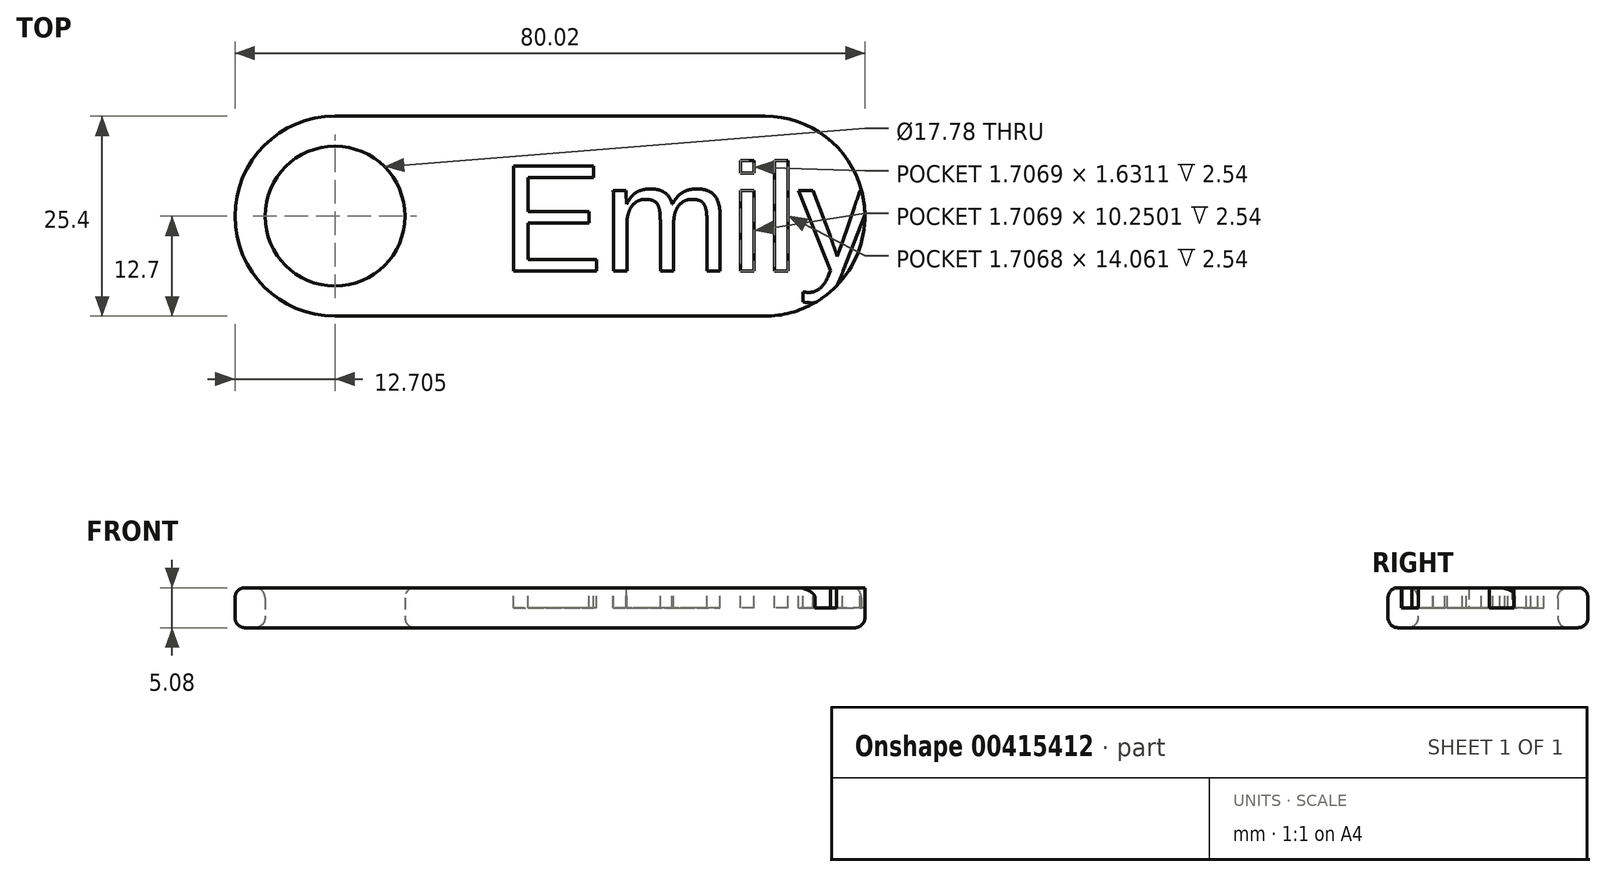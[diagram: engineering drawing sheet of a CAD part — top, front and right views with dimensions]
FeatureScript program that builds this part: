
annotation { "Feature Type Name" : "Feature", "Feature Type Description" : "" }
export const myFeature = defineFeature(function(context is Context, id is Id, definition is map)
    precondition{}
    {
        {
            var Q0;
            Q0=qCreatedBy(makeId("Top.planeOp"),FACE);
            var sketch = newSketch(context, id + "F0", { "sketchPlane" : qUnion([Q0])});
            skLineSegment(sketch, "E0.bottom", {"start": v(27.3, -12.7) * mm, "end": v(-27.3, -12.7) * mm});
            skLineSegment(sketch, "E0.top", {"start": v(27.3, 12.7) * mm, "end": v(-27.3, 12.7) * mm});
            skPoint(sketch, "E0.middle", {"position": v(0, 0) * mm});
            skArc(sketch, "E1", {"start": v(27.3, -12.7) * mm, "mid": v(40, 0) * mm, "end": v(27.3, 12.7) * mm});
            skArc(sketch, "E2", {"start": v(-27.3, 12.7) * mm, "mid": v(-40, 0) * mm, "end": v(-27.3, -12.7) * mm});
            skCircle(sketch, "E3", {"center": v(-27.3, 0) * mm, "radius": 8.9 * mm});
            skSolve(sketch);
        }
        {
            var Q0;
            Q0=makeQuery(id+"F0.imprint","IMPRINT",FACE,{"disambiguationData":[TD([[makeQuery(id+"F0.imprint","IMPRINT",EDGE,{"derivedFrom":sQuery(id+"F0.wireOp",EDGE,"E0.bottom")}),-1.0]])]});
            extrude(context, id + "F1", {"entities" : qUnion([Q0]), "depth" : 5.08 * mm});
        }
        {
            var Q0;
            Q0=makeQuery(id+"F1.opExtrude","CAP_FACE",FACE,{"disambiguationData":[OSD([sQuery(id+"F0.wireOp",EDGE,"E0.bottom"),sQuery(id+"F0.wireOp",EDGE,"E0.top"),sQuery(id+"F0.wireOp",EDGE,"E1"),sQuery(id+"F0.wireOp",EDGE,"E2"),sQuery(id+"F0.wireOp",EDGE,"E3")])],"isStart":false});
            var sketch = newSketch(context, id + "F2", { "sketchPlane" : qUnion([Q0])});
            skText(sketch, "E4", { "text": "Emily", "fontName": "Arimo-Regular.ttf"});
            const initialGuessF2  = {"E4": [-0.0062, -0.00698, 1, 0, 0.01397]};
            skSetInitialGuess(sketch, initialGuessF2);
            skSolve(sketch);
        }
        {
            var Q0;
            Q0=qSketchRegion(id+"F2",true);
            extrude(context, id + "F3", {"entities" : qUnion([Q0]), "operationType" : NewBodyOperationType.REMOVE, "oppositeDirection" : true, "depth" : 2.54 * mm});
        }
        {
            var Q0;
            Q0=makeQuery(id+"F1.opExtrude","CAP_EDGE",EDGE,{"disambiguationData":[OSD([sQuery(id+"F0.wireOp",EDGE,"E2")])],"isStart":false});
            var Q1;
            Q1=makeQuery(id+"F1.opExtrude","CAP_FACE",FACE,{"disambiguationData":[OSD([sQuery(id+"F0.wireOp",EDGE,"E0.bottom"),sQuery(id+"F0.wireOp",EDGE,"E0.top"),sQuery(id+"F0.wireOp",EDGE,"E1"),sQuery(id+"F0.wireOp",EDGE,"E2"),sQuery(id+"F0.wireOp",EDGE,"E3")])],"isStart":true});
            var Q2;
            Q2=makeQuery(id+"F1.opExtrude","CAP_EDGE",EDGE,{"disambiguationData":[OSD([sQuery(id+"F0.wireOp",EDGE,"E3")])],"isStart":false});
            fillet(context, id + "F4", {"entities" : qUnion([Q0, Q1, Q2]), "radius" : 1.27 * mm, "tangentPropagation" : true, "allowEdgeOverflow" : false});
        }
    });
